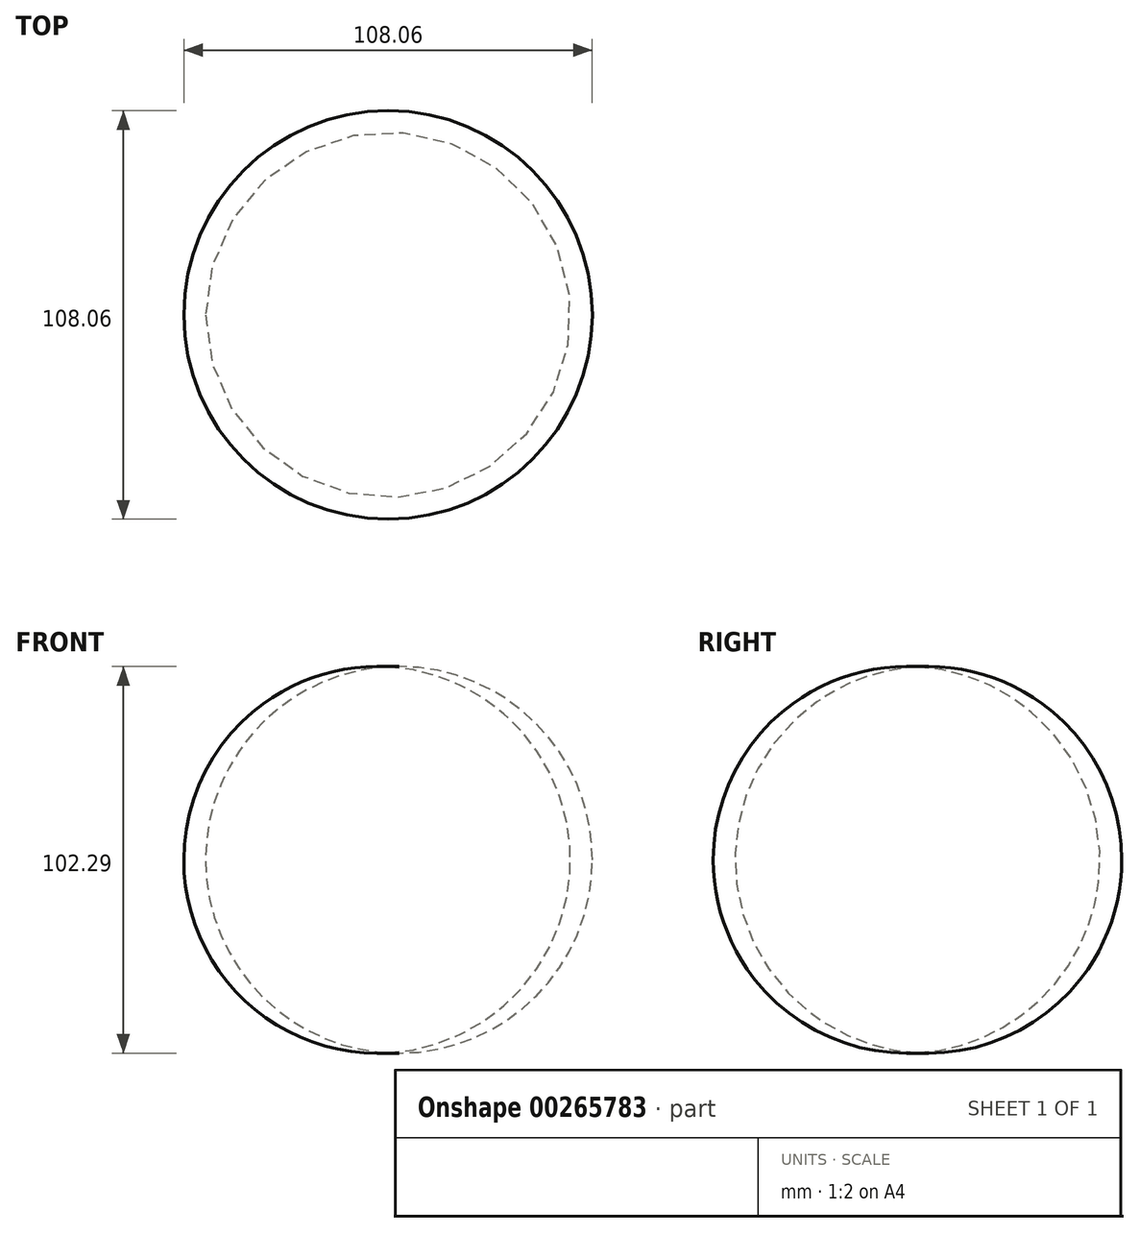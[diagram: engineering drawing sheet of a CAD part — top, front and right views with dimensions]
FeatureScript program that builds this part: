
annotation { "Feature Type Name" : "Feature", "Feature Type Description" : "" }
export const myFeature = defineFeature(function(context is Context, id is Id, definition is map)
    precondition{}
    {
        {
            var Q0;
            Q0=qCreatedBy(makeId("Front.planeOp"),FACE);
            var sketch = newSketch(context, id + "F0", { "sketchPlane" : qUnion([Q0])});
            skArc(sketch, "E0", {"start": v(0, -49.96) * mm, "mid": v(54.03, 1.1) * mm, "end": v(0, 52.17) * mm});
            skLineSegment(sketch, "E1", {"start": v(0, 52.17) * mm, "end": v(0, -49.96) * mm});
            skSolve(sketch);
        }
        {
            var Q0;
            Q0=qCreatedBy(makeId("Front.planeOp"),FACE);
            var sketch = newSketch(context, id + "F1", { "sketchPlane" : qUnion([Q0])});
            skLineSegment(sketch, "E2", {"start": v(0, 57.7) * mm, "end": v(0, -56.23) * mm});
            skSolve(sketch);
        }
        {
            var Q0;
            Q0=makeQuery(id+"F0.imprint","IMPRINT",FACE,{"disambiguationData":[TD([[makeQuery(id+"F0.imprint","IMPRINT",EDGE,{"derivedFrom":sQuery(id+"F0.wireOp",EDGE,"E0")}),1.0]])]});
            var Q1;
            Q1=sQuery(id+"F1.wireOp",EDGE,"E2");
            revolve(context, id + "F2", {"entities" : qUnion([Q0]), "axis" : qUnion([Q1]), "revolveType" : RevolveType.FULL});
        }
    });
